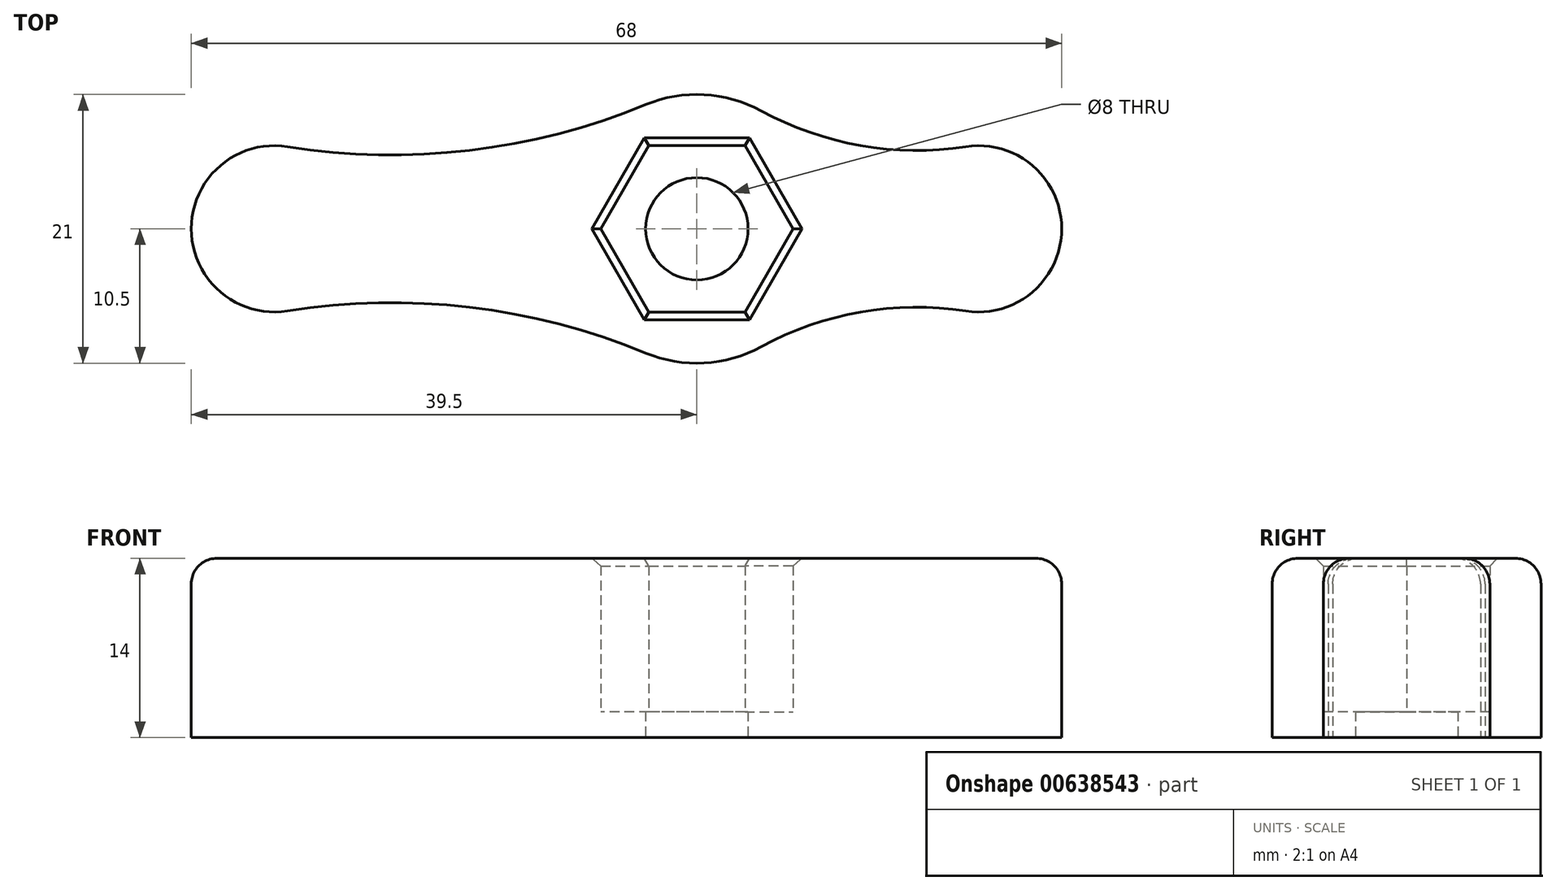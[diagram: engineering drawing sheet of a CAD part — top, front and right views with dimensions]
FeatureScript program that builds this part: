
annotation { "Feature Type Name" : "Feature", "Feature Type Description" : "" }
export const myFeature = defineFeature(function(context is Context, id is Id, definition is map)
    precondition{}
    {
        {
            var Q0;
            Q0=qCreatedBy(makeId("Top.planeOp"),FACE);
            var sketch = newSketch(context, id + "F0", { "sketchPlane" : qUnion([Q0])});
            skCircle(sketch, "E0", {"center": v(-33, 0) * mm, "radius": 6.5 * mm});
            skCircle(sketch, "E1", {"center": v(22, 0) * mm, "radius": 6.5 * mm});
            skCircle(sketch, "E2", {"center": v(0, 0) * mm, "radius": 10.5 * mm});
            skArc(sketch, "E3", {"start": v(-31.98, 6.42) * mm, "mid": v(-17.77, 6.13) * mm, "end": v(-4, 9.7) * mm});
            skArc(sketch, "E4", {"start": v(5.03, 9.22) * mm, "mid": v(12.79, 6.5) * mm, "end": v(21, 6.42) * mm});
            skArc(sketch, "E5.MirrorCS", {"start": v(-31.98, -6.42) * mm, "mid": v(-17.77, -6.13) * mm, "end": v(-4, -9.7) * mm});
            skArc(sketch, "E6.MirrorCS", {"start": v(5.03, -9.22) * mm, "mid": v(12.79, -6.5) * mm, "end": v(21, -6.42) * mm});
            skCircle(sketch, "E7.cCircle", {"center": v(0, 0) * mm, "radius": 6.5 * mm, "construction": true});
            skLineSegment(sketch, "E7.0", {"start": v(7.5, 0) * mm, "end": v(3.75, -6.5) * mm});
            skLineSegment(sketch, "E7.1", {"start": v(3.75, -6.5) * mm, "end": v(-3.75, -6.5) * mm});
            skLineSegment(sketch, "E7.2", {"start": v(-3.75, -6.5) * mm, "end": v(-7.5, 0) * mm});
            skLineSegment(sketch, "E7.3", {"start": v(-7.5, 0) * mm, "end": v(-3.75, 6.5) * mm});
            skLineSegment(sketch, "E7.4", {"start": v(-3.75, 6.5) * mm, "end": v(3.75, 6.5) * mm});
            skLineSegment(sketch, "E7.5", {"start": v(3.75, 6.5) * mm, "end": v(7.5, 0) * mm});
            skPoint(sketch, "E7.0.midPoint", {"position": v(5.63, -3.25) * mm});
            skCircle(sketch, "E8", {"center": v(0, 0) * mm, "radius": 4 * mm});
            skSolve(sketch);
        }
        {
            var Q0;
            {var subQ0=sQuery(id+"F0.wireOp",EDGE,"E0");var subQ1=makeQuery(id+"F0.imprint","INTERSECT",VERTEX,{"derivedFrom":[subQ0,sQuery(id+"F0.wireOp",EDGE,"E3")]});Q0=makeQuery(id+"F0.imprint","IMPRINT",FACE,{"disambiguationData":[TD([[makeQuery(id+"F0.imprint","IMPRINT",EDGE,{"disambiguationData":[TD([[subQ1,-1.0]])],"derivedFrom":subQ0}),1.0]])]});}
            var Q1;
            {var subQ0=sQuery(id+"F0.wireOp",EDGE,"E3");Q1=makeQuery(id+"F0.imprint","IMPRINT",FACE,{"disambiguationData":[TD([[makeQuery(id+"F0.imprint","IMPRINT",EDGE,{"derivedFrom":subQ0}),-1.0]])]});}
            var Q2;
            Q2=makeQuery(id+"F0.imprint","IMPRINT",FACE,{"disambiguationData":[TD([[makeQuery(id+"F0.imprint","IMPRINT",EDGE,{"derivedFrom":sQuery(id+"F0.wireOp",EDGE,"E7.0")}),1.0]])]});
            var Q3;
            {var subQ0=sQuery(id+"F0.wireOp",EDGE,"E4");Q3=makeQuery(id+"F0.imprint","IMPRINT",FACE,{"disambiguationData":[TD([[makeQuery(id+"F0.imprint","IMPRINT",EDGE,{"derivedFrom":subQ0}),-1.0]])]});}
            var Q4;
            {var subQ0=sQuery(id+"F0.wireOp",EDGE,"E1");var subQ1=makeQuery(id+"F0.imprint","INTERSECT",VERTEX,{"derivedFrom":[subQ0,sQuery(id+"F0.wireOp",EDGE,"E4")]});Q4=makeQuery(id+"F0.imprint","IMPRINT",FACE,{"disambiguationData":[TD([[makeQuery(id+"F0.imprint","IMPRINT",EDGE,{"disambiguationData":[TD([[subQ1,-1.0]])],"derivedFrom":subQ0}),1.0]])]});}
            extrude(context, id + "F1", {"entities" : qUnion([Q0, Q1, Q2, Q3, Q4]), "depth" : 14 * mm, "offsetDistance" : 25 * mm});
        }
        {
            var Q0;
            Q0=makeQuery(id+"F0.imprint","IMPRINT",FACE,{"disambiguationData":[TD([[makeQuery(id+"F0.imprint","IMPRINT",EDGE,{"derivedFrom":sQuery(id+"F0.wireOp",EDGE,"E7.0")}),-1.0]])]});
            extrude(context, id + "F2", {"entities" : qUnion([Q0]), "operationType" : NewBodyOperationType.ADD, "depth" : 2 * mm, "offsetDistance" : 25 * mm});
        }
        {
            var Q0;
            Q0=makeQuery(id+"F1.opExtrude","CAP_EDGE",EDGE,{"disambiguationData":[OSD([sQuery(id+"F0.wireOp",EDGE,"E5.MirrorCS")])],"isStart":false});
            fillet(context, id + "F3", {"entities" : qUnion([Q0]), "radius" : 2 * mm, "tangentPropagation" : true, "allowEdgeOverflow" : false});
        }
        {
            var Q0;
            Q0=makeQuery(id+"F1.opExtrude","CAP_EDGE",EDGE,{"disambiguationData":[OSD([sQuery(id+"F0.wireOp",EDGE,"E7.3")])],"isStart":false});
            var Q1;
            Q1=makeQuery(id+"F1.opExtrude","CAP_EDGE",EDGE,{"disambiguationData":[OSD([sQuery(id+"F0.wireOp",EDGE,"E7.4")])],"isStart":false});
            var Q2;
            Q2=makeQuery(id+"F1.opExtrude","CAP_EDGE",EDGE,{"disambiguationData":[OSD([sQuery(id+"F0.wireOp",EDGE,"E7.5")])],"isStart":false});
            var Q3;
            Q3=makeQuery(id+"F1.opExtrude","CAP_EDGE",EDGE,{"disambiguationData":[OSD([sQuery(id+"F0.wireOp",EDGE,"E7.0")])],"isStart":false});
            var Q4;
            Q4=makeQuery(id+"F1.opExtrude","CAP_EDGE",EDGE,{"disambiguationData":[OSD([sQuery(id+"F0.wireOp",EDGE,"E7.1")])],"isStart":false});
            var Q5;
            Q5=makeQuery(id+"F1.opExtrude","CAP_EDGE",EDGE,{"disambiguationData":[OSD([sQuery(id+"F0.wireOp",EDGE,"E7.2")])],"isStart":false});
            chamfer(context, id + "F4", {"entities" : qUnion([Q0, Q1, Q2, Q3, Q4, Q5]), "width" : 0.6 * mm, "tangentPropagation" : true});
        }
    });
